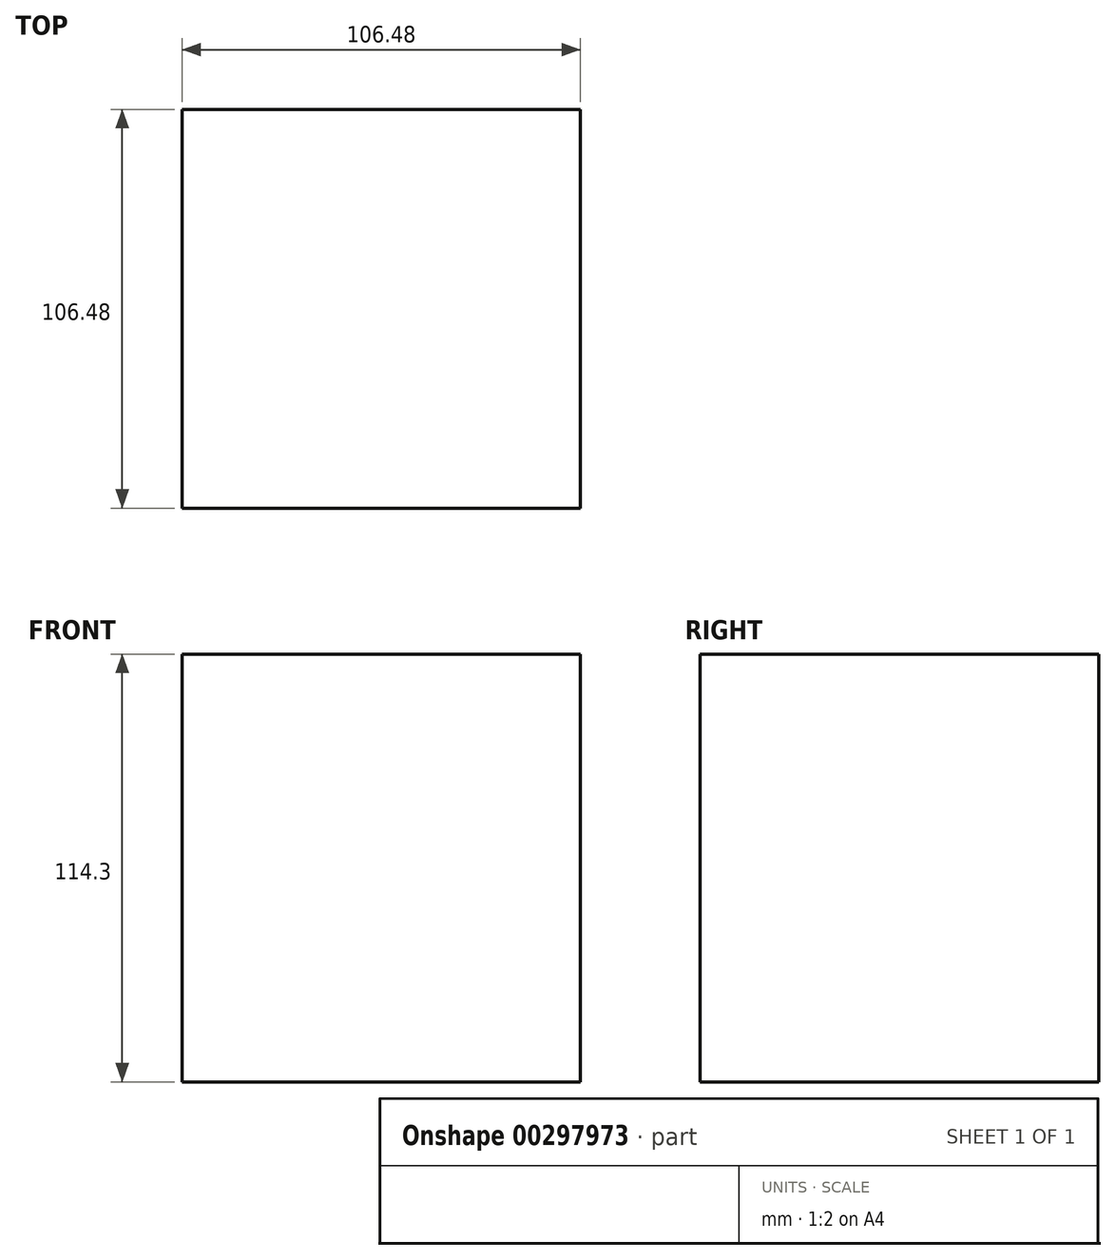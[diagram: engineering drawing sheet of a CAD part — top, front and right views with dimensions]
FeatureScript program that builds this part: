
annotation { "Feature Type Name" : "Feature", "Feature Type Description" : "" }
export const myFeature = defineFeature(function(context is Context, id is Id, definition is map)
    precondition{}
    {
        {
            var Q0;
            Q0=qCreatedBy(makeId("Top.planeOp"),FACE);
            var sketch = newSketch(context, id + "F0", { "sketchPlane" : qUnion([Q0])});
            skLineSegment(sketch, "E0.bottom", {"start": v(-71.38, 48.14) * mm, "end": v(35.1, 48.14) * mm});
            skLineSegment(sketch, "E0.top", {"start": v(-71.38, -58.34) * mm, "end": v(35.1, -58.34) * mm});
            skLineSegment(sketch, "E0.left", {"start": v(-71.38, 48.14) * mm, "end": v(-71.38, -58.34) * mm});
            skLineSegment(sketch, "E0.right", {"start": v(35.1, 48.14) * mm, "end": v(35.1, -58.34) * mm});
            skSolve(sketch);
        }
        {
            var Q0;
            Q0 = qSketchRegion(id + "F0", true);
            extrude(context, id + "F1", {"entities" : qUnion([Q0]), "depth" : 114.3 * mm});
        }
    });
